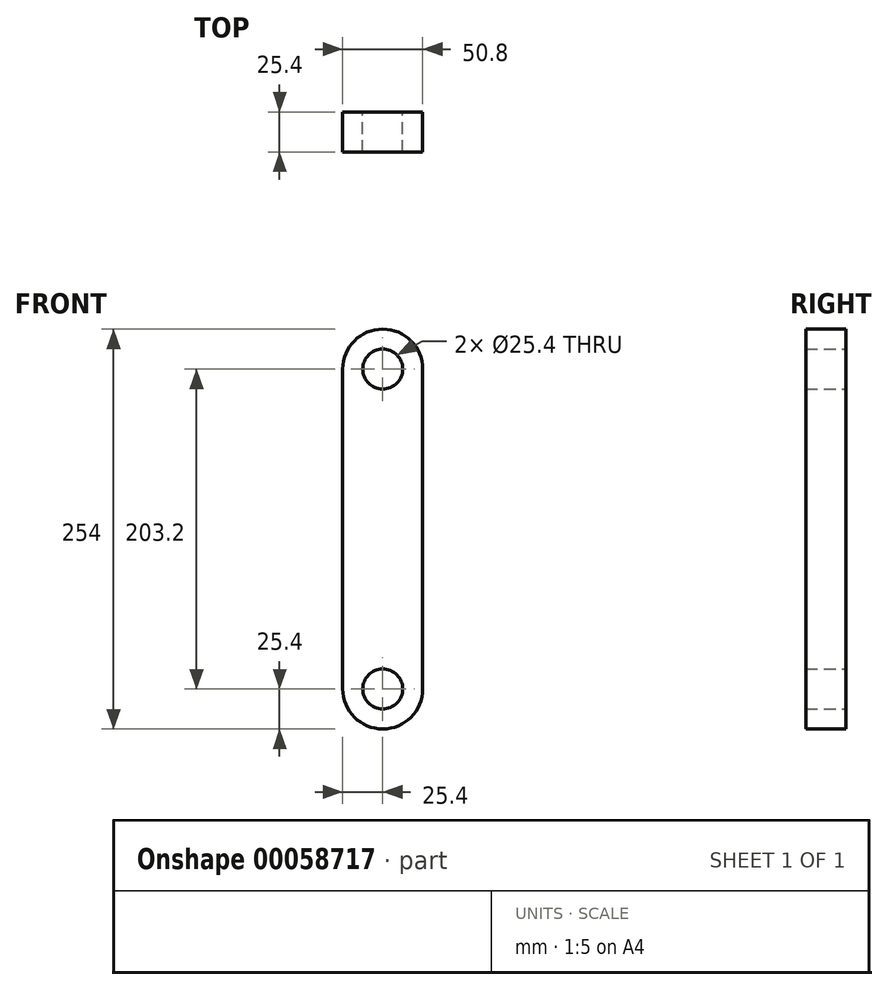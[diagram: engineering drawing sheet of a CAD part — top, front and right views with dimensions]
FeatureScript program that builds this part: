
annotation { "Feature Type Name" : "Feature", "Feature Type Description" : "" }
export const myFeature = defineFeature(function(context is Context, id is Id, definition is map)
    precondition{}
    {
        {
            var Q0;
            Q0=qCreatedBy(makeId("Front.planeOp"),FACE);
            var sketch = newSketch(context, id + "F0", { "sketchPlane" : qUnion([Q0])});
            skCircle(sketch, "E0", {"center": v(0, 0) * mm, "radius": 12.7 * mm});
            skArc(sketch, "E1", {"start": v(25.4, 0) * mm, "mid": v(0, 25.4) * mm, "end": v(-25.4, 0) * mm});
            skCircle(sketch, "E2", {"center": v(0, -203.2) * mm, "radius": 12.7 * mm});
            skArc(sketch, "E3", {"start": v(-25.4, -203.2) * mm, "mid": v(0, -228.6) * mm, "end": v(25.4, -203.2) * mm});
            skLineSegment(sketch, "E4", {"start": v(-25.4, 0) * mm, "end": v(-25.4, -203.2) * mm});
            skLineSegment(sketch, "E5", {"start": v(25.4, 0) * mm, "end": v(25.4, -203.2) * mm});
            skSolve(sketch);
        }
        {
            var Q0;
            Q0=makeQuery(id+"F0.imprint","IMPRINT",FACE,{"disambiguationData":[TD([[makeQuery(id+"F0.imprint","IMPRINT",EDGE,{"derivedFrom":sQuery(id+"F0.wireOp",EDGE,"E0")}),-1.0]])]});
            extrude(context, id + "F1", {"entities" : qUnion([Q0]), "depth" : 25.4 * mm});
        }
    });
